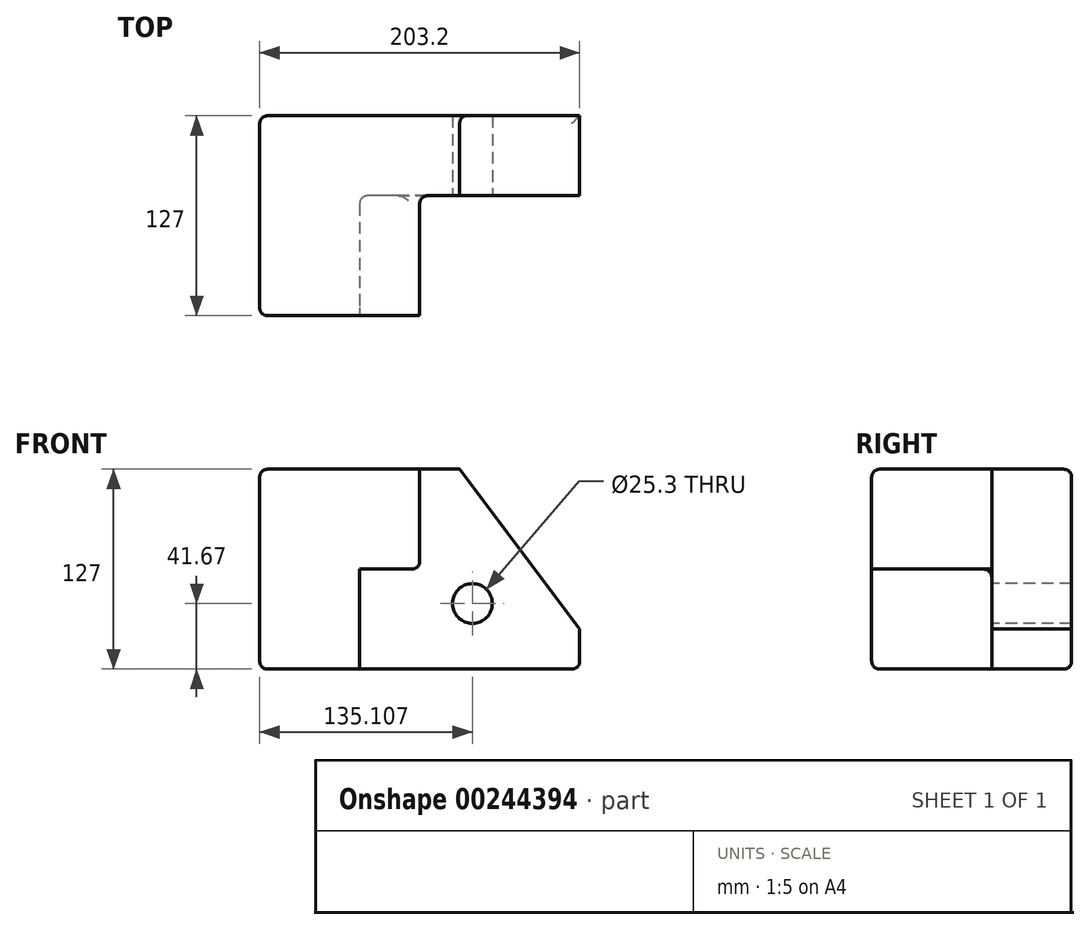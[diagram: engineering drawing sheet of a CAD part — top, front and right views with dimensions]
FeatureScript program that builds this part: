
annotation { "Feature Type Name" : "Feature", "Feature Type Description" : "" }
export const myFeature = defineFeature(function(context is Context, id is Id, definition is map)
    precondition{}
    {
        {
            var Q0;
            Q0=qCreatedBy(makeId("Front.planeOp"),FACE);
            var sketch = newSketch(context, id + "F0", { "sketchPlane" : qUnion([Q0])});
            skLineSegment(sketch, "E0.bottom", {"start": v(101.6, 63.5) * mm, "end": v(-101.6, 63.5) * mm});
            skLineSegment(sketch, "E0.top", {"start": v(101.6, -63.5) * mm, "end": v(-101.6, -63.5) * mm});
            skLineSegment(sketch, "E0.left", {"start": v(101.6, 63.5) * mm, "end": v(101.6, -63.5) * mm});
            skLineSegment(sketch, "E0.right", {"start": v(-101.6, 63.5) * mm, "end": v(-101.6, -63.5) * mm});
            skPoint(sketch, "E0.middle", {"position": v(0, 0) * mm});
            skSolve(sketch);
        }
        {
            var Q0;
            Q0 = qSketchRegion(id + "F0", true);
            extrude(context, id + "F1", {"entities" : qUnion([Q0]), "depth" : 127 * mm});
        }
        {
            var Q0;
            Q0=makeQuery(id+"F1.opExtrude","CAP_FACE",FACE,{"disambiguationData":[OSD([sQuery(id+"F0.wireOp",EDGE,"E0.bottom"),sQuery(id+"F0.wireOp",EDGE,"E0.top"),sQuery(id+"F0.wireOp",EDGE,"E0.left"),sQuery(id+"F0.wireOp",EDGE,"E0.right")])],"isStart":false});
            var sketch = newSketch(context, id + "F2", { "sketchPlane" : qUnion([Q0])});
            skLineSegment(sketch, "E1", {"start": v(0, 63.5) * mm, "end": v(0, 0) * mm});
            skLineSegment(sketch, "E2", {"start": v(-101.6, 63.5) * mm, "end": v(0, 63.5) * mm});
            skLineSegment(sketch, "E3", {"start": v(-101.6, 63.5) * mm, "end": v(-101.6, -63.5) * mm});
            skLineSegment(sketch, "E4", {"start": v(-101.6, -63.5) * mm, "end": v(-38.1, -63.5) * mm});
            skLineSegment(sketch, "E5", {"start": v(0, 0) * mm, "end": v(-38.1, 0) * mm});
            skLineSegment(sketch, "E6", {"start": v(-38.1, 0) * mm, "end": v(-38.1, -63.5) * mm});
            skSolve(sketch);
        }
        {
            var Q0;
            {var subQ2=sQuery(id+"F2.wireOp",EDGE,"E1");Q0=makeQuery(id+"F2.imprint","IMPRINT",FACE,{"disambiguationData":[TD([[makeQuery(id+"F2.imprint","IMPRINT",EDGE,{"derivedFrom":subQ2}),1.0]])]});}
            extrude(context, id + "F3", {"entities" : qUnion([Q0]), "operationType" : NewBodyOperationType.REMOVE, "oppositeDirection" : true, "depth" : 76.2 * mm});
        }
        {
            var Q0;
            Q0=makeQuery(id+"F1.opExtrude","SWEPT_EDGE",EDGE,{"disambiguationData":[OSD([sQuery(id+"F0.wireOp",EDGE,"E0.bottom"),sQuery(id+"F0.wireOp",EDGE,"E0.left")])]});
            chamfer(context, id + "F4", {"entities" : qUnion([Q0]), "chamferType" : ChamferType.TWO_OFFSETS, "width1" : 76.2 * mm, "oppositeDirection" : false, "width2" : 101.6 * mm, "tangentPropagation" : true});
        }
        {
            var Q0;
            Q0=makeQuery(id+"F3.boolean.opBoolean","COPY",EDGE,{"derivedFrom":makeQuery(id+"F3.opExtrude","SWEPT_EDGE",EDGE,{"disambiguationData":[OSD([sQuery(id+"F0.wireOp",EDGE,"E0.bottom"),sQuery(id+"F2.wireOp",EDGE,"E1"),sQuery(id+"F2.wireOp",EDGE,"E2")])]})});
            var Q1;
            Q1=makeQuery(id+"F1.opExtrude","CAP_EDGE",EDGE,{"disambiguationData":[OSD([sQuery(id+"F0.wireOp",EDGE,"E0.bottom")])],"isStart":false});
            var Q2;
            Q2=makeQuery(id+"F3.boolean.opBoolean","COPY",EDGE,{"derivedFrom":makeQuery(id+"F3.opExtrude","CAP_EDGE",EDGE,{"disambiguationData":[OSD([sQuery(id+"F2.wireOp",EDGE,"E5")])],"isStart":true})});
            var Q3;
            Q3=makeQuery(id+"F3.boolean.opBoolean","COPY",EDGE,{"derivedFrom":makeQuery(id+"F3.opExtrude","CAP_EDGE",EDGE,{"disambiguationData":[OSD([sQuery(id+"F2.wireOp",EDGE,"E1")])],"isStart":true})});
            var Q4;
            Q4=makeQuery(id+"F3.boolean.opBoolean","COPY",EDGE,{"derivedFrom":makeQuery(id+"F3.opExtrude","SWEPT_EDGE",EDGE,{"disambiguationData":[OSD([sQuery(id+"F2.wireOp",EDGE,"E1"),sQuery(id+"F2.wireOp",EDGE,"E5")])]})});
            var Q5;
            Q5=makeQuery(id+"F3.boolean.opBoolean","COPY",EDGE,{"derivedFrom":makeQuery(id+"F3.opExtrude","CAP_EDGE",EDGE,{"disambiguationData":[OSD([sQuery(id+"F2.wireOp",EDGE,"E6")])],"isStart":true})});
            var Q6;
            Q6=makeQuery(id+"F3.boolean.opBoolean","COPY",EDGE,{"derivedFrom":makeQuery(id+"F3.opExtrude","SWEPT_EDGE",EDGE,{"disambiguationData":[OSD([sQuery(id+"F0.wireOp",EDGE,"E0.top"),sQuery(id+"F2.wireOp",EDGE,"E4"),sQuery(id+"F2.wireOp",EDGE,"E6")])]})});
            var Q7;
            Q7=makeQuery(id+"F1.opExtrude","CAP_EDGE",EDGE,{"disambiguationData":[OSD([sQuery(id+"F0.wireOp",EDGE,"E0.top")])],"isStart":false});
            var Q8;
            Q8=makeQuery(id+"F3.boolean.opBoolean","COPY",EDGE,{"derivedFrom":makeQuery(id+"F3.opExtrude","CAP_EDGE",EDGE,{"disambiguationData":[OSD([sQuery(id+"F2.wireOp",EDGE,"E1")])],"isStart":false})});
            var Q9;
            Q9=makeQuery(id+"F3.boolean.opBoolean","COPY",EDGE,{"derivedFrom":makeQuery(id+"F3.opExtrude","CAP_EDGE",EDGE,{"disambiguationData":[OSD([sQuery(id+"F0.wireOp",EDGE,"E0.top")])],"isStart":false})});
            var Q10;
            Q10=makeQuery(id+"F3.boolean.opBoolean","COPY",EDGE,{"derivedFrom":makeQuery(id+"F3.opExtrude","CAP_EDGE",EDGE,{"disambiguationData":[OSD([sQuery(id+"F2.wireOp",EDGE,"E6")])],"isStart":false})});
            var Q11;
            Q11=makeQuery(id+"F1.opExtrude","CAP_EDGE",EDGE,{"disambiguationData":[OSD([sQuery(id+"F0.wireOp",EDGE,"E0.top")])],"isStart":true});
            var Q12;
            Q12=makeQuery(id+"F1.opExtrude","CAP_EDGE",EDGE,{"disambiguationData":[OSD([sQuery(id+"F0.wireOp",EDGE,"E0.bottom")])],"isStart":true});
            var Q13;
            Q13=makeQuery(id+"F1.opExtrude","CAP_EDGE",EDGE,{"disambiguationData":[OSD([sQuery(id+"F0.wireOp",EDGE,"E0.right")])],"isStart":false});
            var Q14;
            Q14=makeQuery(id+"F1.opExtrude","SWEPT_EDGE",EDGE,{"disambiguationData":[OSD([sQuery(id+"F0.wireOp",EDGE,"E0.bottom"),sQuery(id+"F0.wireOp",EDGE,"E0.right")])]});
            var Q15;
            Q15=makeQuery(id+"F1.opExtrude","CAP_EDGE",EDGE,{"disambiguationData":[OSD([sQuery(id+"F0.wireOp",EDGE,"E0.right")])],"isStart":true});
            var Q16;
            Q16=makeQuery(id+"F1.opExtrude","SWEPT_EDGE",EDGE,{"disambiguationData":[OSD([sQuery(id+"F0.wireOp",EDGE,"E0.top"),sQuery(id+"F0.wireOp",EDGE,"E0.left")])]});
            var Q17;
            Q17=makeQuery(id+"F1.opExtrude","SWEPT_EDGE",EDGE,{"disambiguationData":[OSD([sQuery(id+"F0.wireOp",EDGE,"E0.top"),sQuery(id+"F0.wireOp",EDGE,"E0.right")])]});
            fillet(context, id + "F5", {"entities" : qUnion([Q0, Q1, Q2, Q3, Q4, Q5, Q6, Q7, Q8, Q9, Q10, Q11, Q12, Q13, Q14, Q15, Q16, Q17]), "radius" : 5.08 * mm, "tangentPropagation" : true, "allowEdgeOverflow" : false});
        }
        {
            var Q0;
            Q0=makeQuery(id+"F3.boolean.opBoolean","COPY",FACE,{"derivedFrom":makeQuery(id+"F3.opExtrude","CAP_FACE",FACE,{"disambiguationData":[OSD([sQuery(id+"F0.wireOp",EDGE,"E0.bottom"),sQuery(id+"F0.wireOp",EDGE,"E0.top"),sQuery(id+"F0.wireOp",EDGE,"E0.left"),sQuery(id+"F2.wireOp",EDGE,"E1"),sQuery(id+"F2.wireOp",EDGE,"E5"),sQuery(id+"F2.wireOp",EDGE,"E6")])],"isStart":false})});
            var sketch = newSketch(context, id + "F6", { "sketchPlane" : qUnion([Q0])});
            skPoint(sketch, "E7.center.orphan", {"position": v(17.78, -17.78) * mm});
            skCircle(sketch, "E8", {"center": v(33.5, -21.83) * mm, "radius": 12.65 * mm});
            skSolve(sketch);
        }
        {
            var Q0;
            Q0=makeQuery(id+"F6.imprint","IMPRINT",FACE,{"disambiguationData":[TD([[makeQuery(id+"F6.imprint","IMPRINT",EDGE,{"derivedFrom":sQuery(id+"F6.wireOp",EDGE,"E8")}),1.0]])]});
            extrude(context, id + "F7", {"entities" : qUnion([Q0]), "operationType" : NewBodyOperationType.REMOVE, "oppositeDirection" : true, "depth" : 78.49 * mm});
        }
    });
